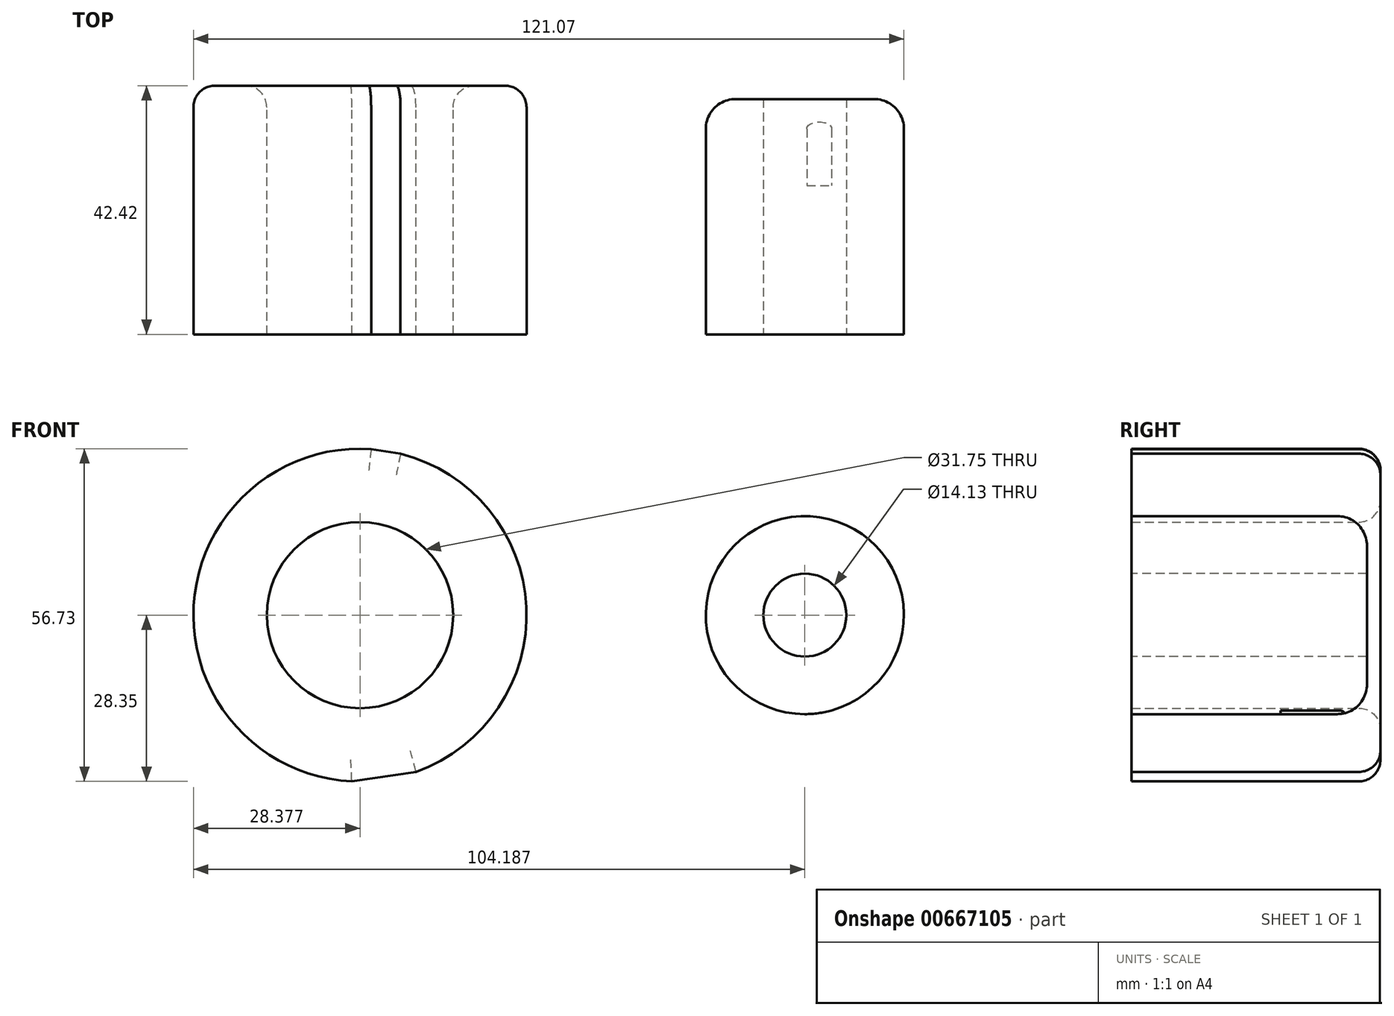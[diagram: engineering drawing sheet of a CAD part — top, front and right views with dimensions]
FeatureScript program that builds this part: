
annotation { "Feature Type Name" : "Feature", "Feature Type Description" : "" }
export const myFeature = defineFeature(function(context is Context, id is Id, definition is map)
    precondition{}
    {
        {
            var Q0;
            Q0=qCreatedBy(makeId("Front.planeOp"),FACE);
            var sketch = newSketch(context, id + "F0", { "sketchPlane" : qUnion([Q0])});
            skLineSegment(sketch, "E0", {"start": v(0, 0) * mm, "end": v(-44.2, 0) * mm});
            skLineSegment(sketch, "E1", {"start": v(-44.2, 0) * mm, "end": v(0, 0) * mm});
            skCircle(sketch, "E2", {"center": v(-44.2, 0) * mm, "radius": 15.88 * mm});
            skCircle(sketch, "E3", {"center": v(-44.2, 0) * mm, "radius": 28.38 * mm});
            skLineSegment(sketch, "E4", {"start": v(0, 0) * mm, "end": v(31.62, 0) * mm});
            skLineSegment(sketch, "E5", {"start": v(31.62, 0) * mm, "end": v(0, 0) * mm});
            skCircle(sketch, "E6", {"center": v(31.62, 0) * mm, "radius": 7.07 * mm});
            skCircle(sketch, "E7", {"center": v(31.62, 0) * mm, "radius": 16.88 * mm});
            skLineSegment(sketch, "E8", {"start": v(-42.3, 28.32) * mm, "end": v(30.4, 16.84) * mm});
            skLineSegment(sketch, "E9", {"start": v(-45.58, -28.35) * mm, "end": v(36.2, -16.25) * mm});
            skSolve(sketch);
        }
        {
            var Q0;
            Q0=makeQuery(id+"F0.imprint","IMPRINT",FACE,{"disambiguationData":[TD([[makeQuery(id+"F0.imprint","IMPRINT",EDGE,{"derivedFrom":sQuery(id+"F0.wireOp",EDGE,"E2")}),1.0]])]});
            var Q1;
            Q1=makeQuery(id+"F0.imprint","IMPRINT",FACE,{"disambiguationData":[TD([[makeQuery(id+"F0.imprint","IMPRINT",EDGE,{"derivedFrom":sQuery(id+"F0.wireOp",EDGE,"E6")}),1.0]])]});
            var Q2;
            {var subQ0=sQuery(id+"F0.wireOp",EDGE,"E8");var subQ1=sQuery(id+"F0.wireOp",EDGE,"E3");var subQ2=makeQuery(id+"F0.imprint","INTERSECT",VERTEX,{"disambiguationData":[OD(0.0)],"derivedFrom":[subQ1,subQ0]});Q2=makeQuery(id+"F0.imprint","IMPRINT",FACE,{"disambiguationData":[TD([[makeQuery(id+"F0.imprint","IMPRINT",EDGE,{"disambiguationData":[TD([[subQ2,1.0]])],"derivedFrom":subQ1}),1.0]])]});}
            var Q3;
            {var subQ3=sQuery(id+"F0.wireOp",EDGE,"E5");var subQ5=sQuery(id+"F0.wireOp",EDGE,"E1");var subQ6=makeQuery(id+"F0.imprint","INTERSECT",VERTEX,{"derivedFrom":[subQ5,subQ3]});Q3=makeQuery(id+"F0.imprint","IMPRINT",FACE,{"disambiguationData":[TD([[makeQuery(id+"F0.imprint","IMPRINT",EDGE,{"disambiguationData":[TD([[subQ6,1.0]])],"derivedFrom":subQ5}),1.0]])]});}
            var Q4;
            Q4=makeQuery(id+"F0.imprint","IMPRINT",FACE,{"disambiguationData":[TD([[makeQuery(id+"F0.imprint","IMPRINT",EDGE,{"derivedFrom":sQuery(id+"F0.wireOp",EDGE,"E6")}),-1.0]])]});
            var Q5;
            {var subQ0=sQuery(id+"F0.wireOp",EDGE,"E5");var subQ1=sQuery(id+"F0.wireOp",EDGE,"E1");var subQ2=makeQuery(id+"F0.imprint","INTERSECT",VERTEX,{"derivedFrom":[subQ1,subQ0]});Q5=makeQuery(id+"F0.imprint","IMPRINT",FACE,{"disambiguationData":[TD([[makeQuery(id+"F0.imprint","IMPRINT",EDGE,{"disambiguationData":[TD([[subQ2,1.0]])],"derivedFrom":subQ1}),-1.0]])]});}
            var Q6;
            {var subQ0=sQuery(id+"F0.wireOp",EDGE,"E9");var subQ1=sQuery(id+"F0.wireOp",EDGE,"E3");var subQ2=makeQuery(id+"F0.imprint","INTERSECT",VERTEX,{"disambiguationData":[OD(0.0)],"derivedFrom":[subQ1,subQ0]});Q6=makeQuery(id+"F0.imprint","IMPRINT",FACE,{"disambiguationData":[TD([[makeQuery(id+"F0.imprint","IMPRINT",EDGE,{"disambiguationData":[TD([[subQ2,-1.0]])],"derivedFrom":subQ1}),1.0]])]});}
            var Q7;
            {var subQ0=sQuery(id+"F0.wireOp",EDGE,"E9");var subQ1=sQuery(id+"F0.wireOp",EDGE,"E7");var subQ2=makeQuery(id+"F0.imprint","INTERSECT",VERTEX,{"disambiguationData":[OD(0.0)],"derivedFrom":[subQ1,subQ0]});Q7=makeQuery(id+"F0.imprint","IMPRINT",FACE,{"disambiguationData":[TD([[makeQuery(id+"F0.imprint","IMPRINT",EDGE,{"disambiguationData":[TD([[subQ2,1.0]])],"derivedFrom":subQ1}),1.0]])]});}
            var Q8;
            Q8=makeQuery(id+"F0.imprint","IMPRINT",FACE,{"disambiguationData":[TD([[makeQuery(id+"F0.imprint","IMPRINT",EDGE,{"derivedFrom":sQuery(id+"F0.wireOp",EDGE,"E2")}),-1.0]])]});
            extrude(context, id + "F1", {"entities" : qUnion([Q0, Q1, Q2, Q3, Q4, Q5, Q6, Q7, Q8]), "depth" : 25.4 * mm, "offsetDistance" : 25.4 * mm});
        }
        {
            var Q0;
            Q0=makeQuery(id+"F0.imprint","IMPRINT",FACE,{"disambiguationData":[TD([[makeQuery(id+"F0.imprint","IMPRINT",EDGE,{"derivedFrom":sQuery(id+"F0.wireOp",EDGE,"E2")}),1.0]])]});
            var Q1;
            Q1=sQuery(id+"F0.wireOp",EDGE,"E2");
            extrude(context, id + "F2", {"entities" : qUnion([Q0]), "operationType" : NewBodyOperationType.REMOVE, "surfaceEntities" : qUnion([Q1]), "endBound" : BoundingType.SYMMETRIC, "depth" : 468.38 * mm, "offsetDistance" : 25.4 * mm});
        }
        {
            var Q0;
            Q0=makeQuery(id+"F0.imprint","IMPRINT",FACE,{"disambiguationData":[TD([[makeQuery(id+"F0.imprint","IMPRINT",EDGE,{"derivedFrom":sQuery(id+"F0.wireOp",EDGE,"E6")}),1.0]])]});
            var Q1;
            Q1=sQuery(id+"F0.wireOp",EDGE,"E6");
            extrude(context, id + "F3", {"entities" : qUnion([Q0]), "operationType" : NewBodyOperationType.REMOVE, "surfaceEntities" : qUnion([Q1]), "endBound" : BoundingType.SYMMETRIC, "oppositeDirection" : true, "depth" : 60.45 * mm, "offsetDistance" : 25.4 * mm});
        }
        {
            var Q0;
            Q0=makeQuery(id+"F0.imprint","IMPRINT",FACE,{"disambiguationData":[TD([[makeQuery(id+"F0.imprint","IMPRINT",EDGE,{"derivedFrom":sQuery(id+"F0.wireOp",EDGE,"E2")}),-1.0]])]});
            extrude(context, id + "F4", {"entities" : qUnion([Q0]), "operationType" : NewBodyOperationType.ADD, "endBound" : BoundingType.SYMMETRIC, "oppositeDirection" : true, "depth" : 34.04 * mm, "offsetDistance" : 25.4 * mm});
        }
        {
            var Q0;
            Q0=makeQuery(id+"F0.imprint","IMPRINT",FACE,{"disambiguationData":[TD([[makeQuery(id+"F0.imprint","IMPRINT",EDGE,{"derivedFrom":sQuery(id+"F0.wireOp",EDGE,"E6")}),-1.0]])]});
            extrude(context, id + "F5", {"entities" : qUnion([Q0]), "operationType" : NewBodyOperationType.ADD, "oppositeDirection" : true, "depth" : 14.73 * mm, "offsetDistance" : 25.4 * mm});
        }
        {
            var Q0;
            Q0=makeQuery(id+"F4.opExtrude","CAP_FACE",FACE,{"disambiguationData":[OSD([sQuery(id+"F0.wireOp",EDGE,"E2"),sQuery(id+"F0.wireOp",EDGE,"E3"),sQuery(id+"F0.wireOp",EDGE,"E8"),sQuery(id+"F0.wireOp",EDGE,"E9")])],"isStart":false});
            fillet(context, id + "F6", {"entities" : qUnion([Q0]), "radius" : 3.68 * mm, "tangentPropagation" : true, "allowEdgeOverflow" : false});
        }
        {
            var Q0;
            Q0=makeQuery(id+"F5.opExtrude","CAP_EDGE",EDGE,{"disambiguationData":[OSD([sQuery(id+"F0.wireOp",EDGE,"E7")])],"isStart":false});
            fillet(context, id + "F7", {"entities" : qUnion([Q0]), "radius" : 5.08 * mm, "tangentPropagation" : true, "allowEdgeOverflow" : false});
        }
    });
